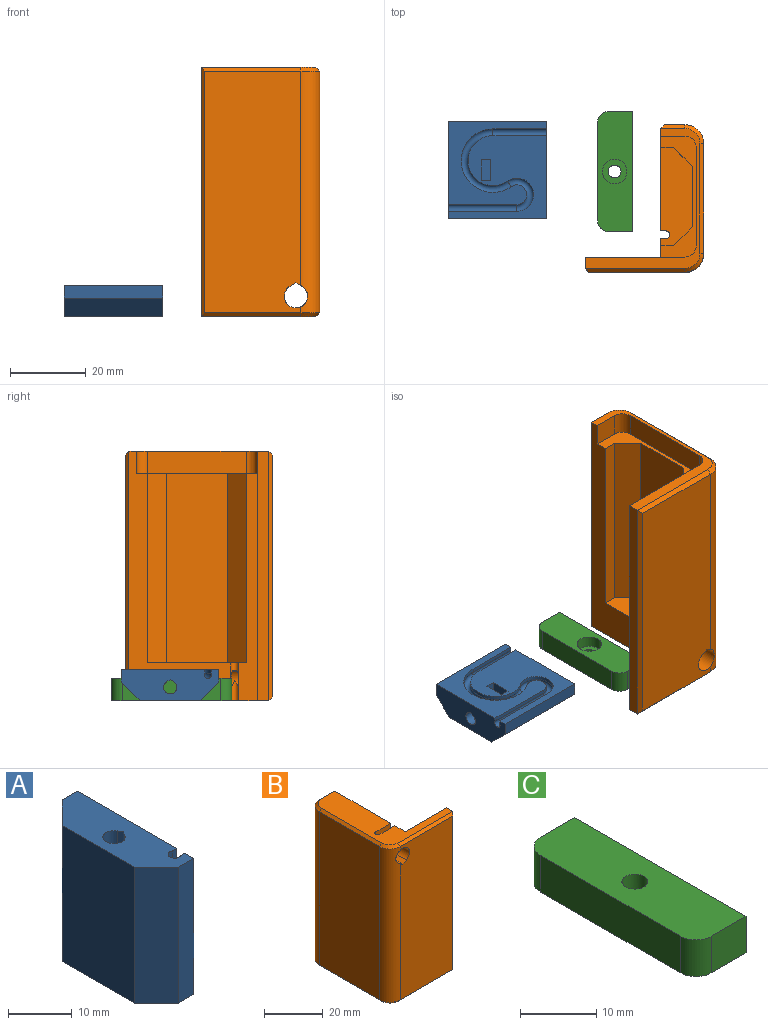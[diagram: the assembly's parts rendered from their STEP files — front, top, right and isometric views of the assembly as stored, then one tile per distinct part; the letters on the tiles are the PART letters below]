
ASSEMBLY  parts=3 mates=2
PART A: 32 faces, bbox 8.3x25.8x26 mm
  f0: plane 25.8x8.3mm, normal (0,0,1), area 175.8mm2, adj f4,f5,f6,f7,f8,f18,f19,f20
  f1: plane 25.8x8.3mm, normal (0,0,-1), area 175.8mm2, adj f4,f5,f6,f7,f8,f9,f10,f11
  f2: plane 7.6x5.5mm, normal (0,0,-1), area 32mm2, adj f4,f21,f22,f23,f27,f28,f29
  f3: plane 7.6x5.5mm, normal (0,0,1), area 32mm2, adj f4,f21,f22,f23,f24,f25,f26
  f4: plane 26x22mm, normal (1,0,0), area 311.2mm2, adj f0,f1,f2,f3,f6,f9,f12,f15
  f5: plane 26x22mm, normal (1,0,0), area 213.9mm2, adj f0,f1,f7,f11,f14,f17,f20
  f6: plane 26x3.36mm, normal (0,1,0), area 87.3mm2, adj f0,f1,f4,f31
  f7: plane 26x3.36mm, normal (0,-1,0), area 87.3mm2, adj f0,f1,f5,f30
  f8: plane 26x15.92mm, normal (-1,0,0), area 413.8mm2, adj f0,f1,f30,f31
  f9: plane 18.16x0.96mm, normal (0,-1,0), area 17.5mm2, adj f1,f4,f10,f12
  f10: cylinder r=1mm len=18.16mm, axis (0,0,1), area 73.4mm2, adj f1,f9,f11,f13
  f11: plane 18.16x0.96mm, normal (0,1,0), area 17.5mm2, adj f1,f5,f10,f14
  f12: cylinder r=4.4mm len=8.8mm, axis (1,0,0), area 15.9mm2, adj f4,f9,f13,f15
  f13: torus R=3.5mm, axis (1,0,0), area 53.1mm2, adj f10,f12,f14,f16
  f14: cylinder r=2.6mm len=5.2mm, axis (1,0,0), area 9.4mm2, adj f5,f11,f13,f17
  f15: cylinder r=6.6mm len=13.2mm, axis (-1,0,0), area 23.9mm2, adj f4,f12,f16,f18
  f16: torus R=7.5mm, axis (-1,0,0), area 113.9mm2, adj f13,f15,f17,f19
  f17: cylinder r=8.4mm len=16.8mm, axis (-1,0,0), area 30.4mm2, adj f5,f14,f16,f20
  f18: plane 14.16x0.96mm, normal (0,-1,0), area 13.7mm2, adj f0,f4,f15,f19
  f19: cylinder r=1mm len=14.16mm, axis (0,0,1), area 57.3mm2, adj f0,f16,f18,f20
  f20: plane 14.16x0.96mm, normal (0,1,0), area 13.7mm2, adj f0,f5,f17,f19
  f21: plane 5.5x2.4mm, normal (1,0,0), area 13.2mm2, adj f2,f3,f22,f23
  f22: plane 7.6x2.4mm, normal (0,1,0), area 18.2mm2, adj f2,f3,f4,f21
  f23: plane 7.6x2.4mm, normal (0,-1,0), area 18.2mm2, adj f2,f3,f4,f21
  f24: plane 8.84x0.88mm, normal (-0.87,-0.5,0), area 8.9mm2, adj f1,f3,f25,f26
  f25: plane 8.84x0.88mm, normal (-0.87,0.5,0), area 8.9mm2, adj f1,f3,f24,f26
  f26: cylinder r=1.75mm len=8.84mm, axis (0,0,-1), area 81mm2, adj f1,f3,f24,f25
  f27: cylinder r=1.75mm len=14.76mm, axis (0,0,-1), area 135.3mm2, adj f0,f2,f28,f29
  f28: plane 14.76x0.88mm, normal (-0.87,0.5,0), area 14.9mm2, adj f0,f2,f27,f29
  f29: plane 14.76x0.88mm, normal (-0.87,-0.5,0), area 14.9mm2, adj f0,f2,f27,f28
  f30: plane 26x4.94mm, normal (-0.71,-0.71,0), area 181.7mm2, adj f0,f1,f7,f8
  f31: plane 26x4.94mm, normal (-0.71,0.71,0), area 181.7mm2, adj f0,f1,f6,f8
PART B: 44 faces, bbox 32x39.6x66.6 mm
  f0: plane 0.15x0.01mm, normal (0,0,1), area 0mm2, adj f41,f42
  f1: plane 0.15x0.01mm, normal (0,0,1), area 0mm2, adj f39,f42
  f2: plane 66x27mm, normal (1,0,0), area 532mm2, adj f4,f5,f10,f15,f17,f19,f26,f39
  f3: plane 60x5mm, normal (1,0,0), area 200mm2, adj f4,f5,f11,f16,f17,f41
  f4: plane 37x30.4mm, normal (0,0,1), area 422mm2, adj f2,f3,f9,f16,f24,f25,f27,f29
  f5: plane 26x8.4mm, normal (0,0,-1), area 189mm2, adj f2,f3,f11,f12,f13,f14,f15,f39
  f6: plane 64x5.4mm, normal (0,1,0), area 322.2mm2, adj f22,f24,f26,f28,f36,f37,f38
  f7: plane 64x29mm, normal (-1,0,0), area 1856mm2, adj f22,f23,f27,f32
  f8: plane 64x25.4mm, normal (0,-1,0), area 1602.2mm2, adj f23,f31,f33,f35,f36,f37,f38
  f9: plane 66x3mm, normal (1,0,0), area 198mm2, adj f4,f10,f16,f33
  f10: plane 37x30.4mm, normal (0,0,-1), area 141mm2, adj f2,f9,f16,f18,f19,f20,f21,f28
  f11: plane 50x3.4mm, normal (0,1,0), area 170mm2, adj f3,f5,f12,f17
  f12: plane 50x5mm, normal (0.71,0.71,0), area 353.6mm2, adj f5,f11,f13,f17
  f13: plane 50x16mm, normal (1,0,0), area 800mm2, adj f5,f12,f14,f17
  f14: plane 50x5mm, normal (0.71,-0.71,0), area 353.6mm2, adj f5,f13,f15,f17
  f15: plane 50x3.4mm, normal (0,-1,0), area 170mm2, adj f2,f5,f14,f17
  f16: plane 66x26.4mm, normal (0,1,0), area 1358.4mm2, adj f3,f4,f9,f10,f17,f20
  f17: plane 32x9.4mm, normal (0,0,-1), area 103.5mm2, adj f2,f3,f11,f12,f13,f14,f15,f16
  f18: plane 26x6mm, normal (1,0,0), area 156mm2, adj f10,f17,f20,f21
  f19: plane 6.4x6mm, normal (0,-1,0), area 38.4mm2, adj f2,f10,f17,f21
  f20: cylinder r=3mm len=6mm, axis (0,0,-1), area 28.3mm2, adj f10,f16,f17,f18
  f21: cylinder r=3mm len=6mm, axis (0,0,-1), area 28.3mm2, adj f10,f17,f18,f19
  f22: cylinder r=5mm len=64mm, axis (0,0,-1), area 495.3mm2, adj f6,f7,f25,f30,f36,f37
  f23: cylinder r=5mm len=64mm, axis (0,0,-1), area 495.3mm2, adj f7,f8,f29,f34,f36,f37
  f24: plane 6.4x1mm, normal (0,0.71,0.71), area 8.3mm2, adj f4,f6,f25,f26
  f25: cone r=4mm half-angle=45deg, axis (0,0,-1), area 10mm2, adj f4,f22,f24,f27
  f26: plane 66x1mm, normal (0.71,0.71,0), area 91.9mm2, adj f2,f6,f24,f28
  f27: plane 29x1mm, normal (-0.71,0,0.71), area 41mm2, adj f4,f7,f25,f29
  f28: plane 6.4x1mm, normal (0,0.71,-0.71), area 8.3mm2, adj f6,f10,f26,f30
  f29: cone r=4mm half-angle=45deg, axis (0,0,-1), area 10mm2, adj f4,f23,f27,f31
  f30: cone r=4mm half-angle=45deg, axis (0,0,1), area 10mm2, adj f10,f22,f28,f32
  f31: plane 26.4x1mm, normal (0,-0.71,0.71), area 36.6mm2, adj f4,f8,f29,f33
  f32: plane 29x1mm, normal (-0.71,0,-0.71), area 41mm2, adj f7,f10,f30,f34
  f33: plane 66x1mm, normal (0.71,-0.71,0), area 91.9mm2, adj f8,f9,f31,f35
  f34: cone r=4mm half-angle=45deg, axis (0,0,1), area 10mm2, adj f10,f23,f32,f35
  f35: plane 26.4x1mm, normal (0,-0.71,-0.71), area 36.6mm2, adj f8,f10,f33,f34
  f36: cylinder r=3.1mm len=39mm, axis (0,-1,0), area 608.6mm2, adj f6,f8,f22,f23,f37,f38,f39,f40
  f37: plane 39x1.55mm, normal (0.5,0,0.87), area 69.8mm2, adj f6,f8,f22,f23,f36,f38
  f38: plane 39x1.55mm, normal (-0.5,0,0.87), area 69.8mm2, adj f6,f8,f36,f37
  f39: plane 10.56x7.76mm, normal (0,-1,0), area 31.1mm2, adj f1,f2,f4,f5,f36,f40,f42,f43
  f40: cylinder r=1mm len=5.42mm, axis (0,0,1), area 13.4mm2, adj f4,f36,f39,f41
  f41: plane 10.56x7.76mm, normal (0,1,0), area 31.1mm2, adj f0,f3,f4,f5,f36,f40,f42,f43
  f42: cylinder r=1mm len=4.58mm, axis (0,0,1), area 8.4mm2, adj f0,f1,f5,f39,f41,f43
  f43: bspline ~4.84x2.77mm, area 5.8mm2, adj f36,f39,f41,f42
PART C: 11 faces, bbox 9.3x31.8x5.9 mm
  f0: plane 31.8x9.3mm, normal (0,0,-1), area 258.9mm2, adj f1,f5,f6,f7,f8,f9,f10
  f1: plane 31.8x5.9mm, normal (1,0,0), area 187.6mm2, adj f0,f2,f6,f8
  f2: plane 31.8x9.3mm, normal (0,0,1), area 283.1mm2, adj f1,f3,f6,f7,f8,f9,f10
  f3: cylinder r=1.7mm len=3.4mm, axis (0,0,-1), area 31mm2, adj f2,f4
  f4: plane 6.5x6.5mm, normal (0,0,-1), area 24.1mm2, adj f3,f5
  f5: cylinder r=3.25mm len=6.5mm, axis (0,0,-1), area 61.3mm2, adj f0,f4
  f6: plane 6.4x5.9mm, normal (0,-1,0), area 37.8mm2, adj f0,f1,f2,f9
  f7: plane 26x5.9mm, normal (-1,0,0), area 153.4mm2, adj f0,f2,f9,f10
  f8: plane 6.4x5.9mm, normal (0,1,0), area 37.8mm2, adj f0,f1,f2,f10
  f9: cylinder r=2.9mm len=5.9mm, axis (0,0,-1), area 26.9mm2, adj f0,f2,f6,f7
  f10: cylinder r=2.9mm len=5.9mm, axis (0,0,-1), area 26.9mm2, adj f0,f2,f7,f8
PLACE A rot(axis=(-0.71,0,-0.71),180deg) t=(-34.84,7.08,4.11)mm
PLACE B rot(axis=(0,1,0),180deg) t=(21.36,0,55.81)mm fixed
PLACE C rot(axis=(1,0,0),180deg) t=(13.94,6.71,-4.29)mm
MATE planar B.f22 <-> A.f8  axis (0,0,-1) through (27.76,14,-4.19)mm
MATE planar B.f4 <-> C.f9  axis (0,0,-1) through (21.36,-13.5,-4.19)mm
